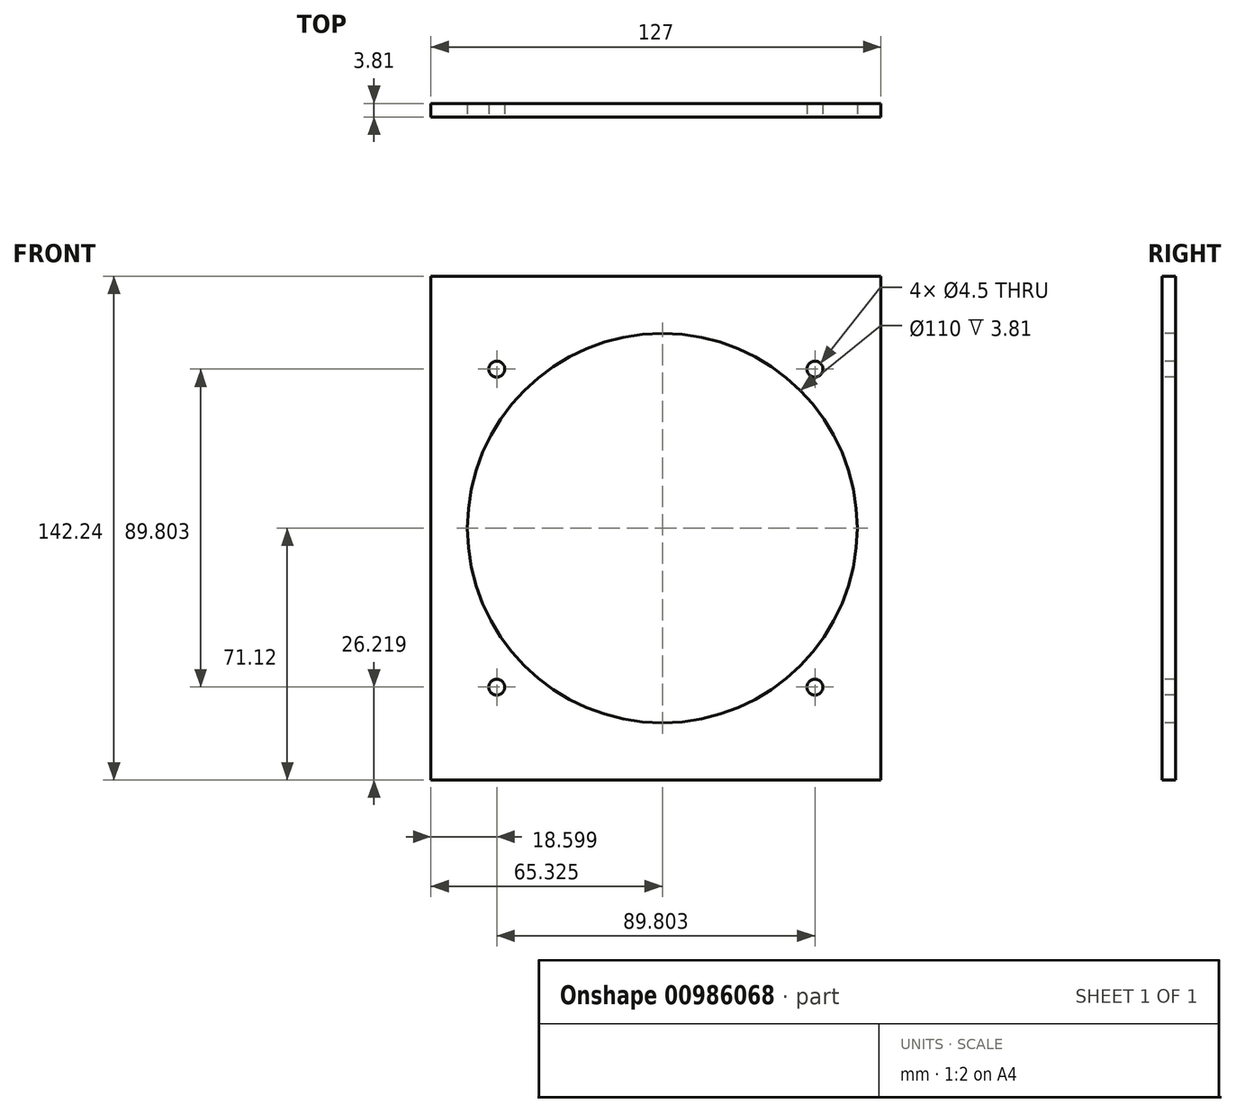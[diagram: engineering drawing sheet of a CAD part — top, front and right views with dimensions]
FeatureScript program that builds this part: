
annotation { "Feature Type Name" : "Feature", "Feature Type Description" : "" }
export const myFeature = defineFeature(function(context is Context, id is Id, definition is map)
    precondition{}
    {
        {
            var Q0;
            Q0=qCreatedBy(makeId("Front.planeOp"),FACE);
            var sketch = newSketch(context, id + "F0", { "sketchPlane" : qUnion([Q0])});
            skLineSegment(sketch, "E0.bottom", {"start": v(63.5, 71.12) * mm, "end": v(-63.5, 71.12) * mm});
            skLineSegment(sketch, "E0.top", {"start": v(63.5, -71.12) * mm, "end": v(-63.5, -71.12) * mm});
            skLineSegment(sketch, "E0.left", {"start": v(63.5, 71.12) * mm, "end": v(63.5, -71.12) * mm});
            skLineSegment(sketch, "E0.right", {"start": v(-63.5, 71.12) * mm, "end": v(-63.5, -71.12) * mm});
            skPoint(sketch, "E0.middle", {"position": v(0, 0) * mm});
            skSolve(sketch);
        }
        {
            var Q0;
            Q0=makeQuery(id+"F0.imprint","IMPRINT",FACE,{"disambiguationData":[TD([[makeQuery(id+"F0.imprint","IMPRINT",EDGE,{"derivedFrom":sQuery(id+"F0.wireOp",EDGE,"E0.bottom")}),1.0]])]});
            extrude(context, id + "F1", {"entities" : qUnion([Q0]), "depth" : 3.8 * mm, "offsetDistance" : 25.4 * mm});
        }
        {
            var Q0;
            Q0=makeQuery(id+"F1.opExtrude","CAP_FACE",FACE,{"disambiguationData":[OSD([sQuery(id+"F0.wireOp",EDGE,"E0.bottom"),sQuery(id+"F0.wireOp",EDGE,"E0.top"),sQuery(id+"F0.wireOp",EDGE,"E0.left"),sQuery(id+"F0.wireOp",EDGE,"E0.right")])],"isStart":false});
            var sketch = newSketch(context, id + "F2", { "sketchPlane" : qUnion([Q0])});
            skCircle(sketch, "E1", {"center": v(1.82, 0) * mm, "radius": 55 * mm});
            skSolve(sketch);
        }
        {
            var Q0;
            Q0=makeQuery(id+"F2.imprint","IMPRINT",FACE,{"disambiguationData":[TD([[makeQuery(id+"F2.imprint","IMPRINT",EDGE,{"derivedFrom":sQuery(id+"F2.wireOp",EDGE,"E1")}),1.0]])]});
            extrude(context, id + "F3", {"entities" : qUnion([Q0]), "operationType" : NewBodyOperationType.REMOVE, "endBound" : BoundingType.UP_TO_NEXT, "oppositeDirection" : true, "depth" : 25.4 * mm, "offsetDistance" : 25.4 * mm});
        }
        {
            var Q0;
            Q0=makeQuery(id+"F1.opExtrude","CAP_FACE",FACE,{"disambiguationData":[OSD([sQuery(id+"F0.wireOp",EDGE,"E0.bottom"),sQuery(id+"F0.wireOp",EDGE,"E0.top"),sQuery(id+"F0.wireOp",EDGE,"E0.left"),sQuery(id+"F0.wireOp",EDGE,"E0.right")])],"isStart":false});
            var sketch = newSketch(context, id + "F4", { "sketchPlane" : qUnion([Q0])});
            skCircle(sketch, "E2", {"center": v(0, 0) * mm, "radius": 63.5 * mm});
            skCircle(sketch, "E3", {"center": v(44.9, -44.9) * mm, "radius": 2.25 * mm});
            skCircle(sketch, "E4", {"center": v(-44.9, -44.9) * mm, "radius": 2.25 * mm});
            skCircle(sketch, "E5", {"center": v(-44.9, 44.9) * mm, "radius": 2.25 * mm});
            skCircle(sketch, "E6", {"center": v(44.9, 44.9) * mm, "radius": 2.25 * mm});
            skLineSegment(sketch, "E7", {"start": v(-44.9, 44.9) * mm, "end": v(0, 0) * mm});
            skLineSegment(sketch, "E8", {"start": v(44.9, 44.9) * mm, "end": v(0, 0) * mm});
            skLineSegment(sketch, "E9", {"start": v(0, 0) * mm, "end": v(44.9, -44.9) * mm});
            skLineSegment(sketch, "E10", {"start": v(0, 0) * mm, "end": v(-44.9, -44.9) * mm});
            skSolve(sketch);
        }
        {
            var Q0;
            {var subQ0=sQuery(id+"F4.wireOp",EDGE,"E7");var subQ1=sQuery(id+"F4.wireOp",EDGE,"E2");var subQ2=makeQuery(id+"F4.imprint","INTERSECT",VERTEX,{"derivedFrom":[subQ1,subQ0]});Q0=makeQuery(id+"F4.imprint","IMPRINT",FACE,{"disambiguationData":[TD([[makeQuery(id+"F4.imprint","IMPRINT",EDGE,{"disambiguationData":[TD([[subQ2,1.0]])],"derivedFrom":subQ1}),1.0]])]});}
            var Q1;
            {var subQ0=sQuery(id+"F4.wireOp",EDGE,"E2");var subQ1=makeQuery(id+"F4.imprint","INTERSECT",VERTEX,{"derivedFrom":[subQ0,sQuery(id+"F4.wireOp",EDGE,"E7")]});Q1=makeQuery(id+"F4.imprint","IMPRINT",FACE,{"disambiguationData":[TD([[makeQuery(id+"F4.imprint","IMPRINT",EDGE,{"disambiguationData":[TD([[subQ1,1.0]])],"derivedFrom":subQ0}),-1.0]])]});}
            var Q2;
            {var subQ0=sQuery(id+"F4.wireOp",EDGE,"E7");var subQ1=sQuery(id+"F4.wireOp",EDGE,"E2");var subQ2=makeQuery(id+"F4.imprint","INTERSECT",VERTEX,{"derivedFrom":[subQ1,subQ0]});Q2=makeQuery(id+"F4.imprint","IMPRINT",FACE,{"disambiguationData":[TD([[makeQuery(id+"F4.imprint","IMPRINT",EDGE,{"disambiguationData":[TD([[subQ2,-1.0]])],"derivedFrom":subQ1}),1.0]])]});}
            var Q3;
            {var subQ0=sQuery(id+"F4.wireOp",EDGE,"E2");var subQ1=makeQuery(id+"F4.imprint","INTERSECT",VERTEX,{"derivedFrom":[subQ0,sQuery(id+"F4.wireOp",EDGE,"E8")]});Q3=makeQuery(id+"F4.imprint","IMPRINT",FACE,{"disambiguationData":[TD([[makeQuery(id+"F4.imprint","IMPRINT",EDGE,{"disambiguationData":[TD([[subQ1,1.0]])],"derivedFrom":subQ0}),-1.0]])]});}
            var Q4;
            {var subQ0=sQuery(id+"F4.wireOp",EDGE,"E8");var subQ1=sQuery(id+"F4.wireOp",EDGE,"E2");var subQ2=makeQuery(id+"F4.imprint","INTERSECT",VERTEX,{"derivedFrom":[subQ1,subQ0]});Q4=makeQuery(id+"F4.imprint","IMPRINT",FACE,{"disambiguationData":[TD([[makeQuery(id+"F4.imprint","IMPRINT",EDGE,{"disambiguationData":[TD([[subQ2,-1.0]])],"derivedFrom":subQ1}),1.0]])]});}
            var Q5;
            {var subQ0=sQuery(id+"F4.wireOp",EDGE,"E8");var subQ1=sQuery(id+"F4.wireOp",EDGE,"E2");var subQ2=makeQuery(id+"F4.imprint","INTERSECT",VERTEX,{"derivedFrom":[subQ1,subQ0]});Q5=makeQuery(id+"F4.imprint","IMPRINT",FACE,{"disambiguationData":[TD([[makeQuery(id+"F4.imprint","IMPRINT",EDGE,{"disambiguationData":[TD([[subQ2,1.0]])],"derivedFrom":subQ1}),1.0]])]});}
            var Q6;
            {var subQ0=sQuery(id+"F4.wireOp",EDGE,"E9");var subQ1=sQuery(id+"F4.wireOp",EDGE,"E2");var subQ2=makeQuery(id+"F4.imprint","INTERSECT",VERTEX,{"derivedFrom":[subQ1,subQ0]});Q6=makeQuery(id+"F4.imprint","IMPRINT",FACE,{"disambiguationData":[TD([[makeQuery(id+"F4.imprint","IMPRINT",EDGE,{"disambiguationData":[TD([[subQ2,1.0]])],"derivedFrom":subQ1}),1.0]])]});}
            var Q7;
            {var subQ0=sQuery(id+"F4.wireOp",EDGE,"E9");var subQ1=sQuery(id+"F4.wireOp",EDGE,"E2");var subQ2=makeQuery(id+"F4.imprint","INTERSECT",VERTEX,{"derivedFrom":[subQ1,subQ0]});Q7=makeQuery(id+"F4.imprint","IMPRINT",FACE,{"disambiguationData":[TD([[makeQuery(id+"F4.imprint","IMPRINT",EDGE,{"disambiguationData":[TD([[subQ2,-1.0]])],"derivedFrom":subQ1}),1.0]])]});}
            var Q8;
            {var subQ0=sQuery(id+"F4.wireOp",EDGE,"E2");var subQ1=makeQuery(id+"F4.imprint","INTERSECT",VERTEX,{"derivedFrom":[subQ0,sQuery(id+"F4.wireOp",EDGE,"E9")]});Q8=makeQuery(id+"F4.imprint","IMPRINT",FACE,{"disambiguationData":[TD([[makeQuery(id+"F4.imprint","IMPRINT",EDGE,{"disambiguationData":[TD([[subQ1,1.0]])],"derivedFrom":subQ0}),-1.0]])]});}
            var Q9;
            {var subQ0=sQuery(id+"F4.wireOp",EDGE,"E2");var subQ1=makeQuery(id+"F4.imprint","INTERSECT",VERTEX,{"derivedFrom":[subQ0,sQuery(id+"F4.wireOp",EDGE,"E10")]});Q9=makeQuery(id+"F4.imprint","IMPRINT",FACE,{"disambiguationData":[TD([[makeQuery(id+"F4.imprint","IMPRINT",EDGE,{"disambiguationData":[TD([[subQ1,1.0]])],"derivedFrom":subQ0}),-1.0]])]});}
            var Q10;
            {var subQ0=sQuery(id+"F4.wireOp",EDGE,"E10");var subQ1=sQuery(id+"F4.wireOp",EDGE,"E2");var subQ2=makeQuery(id+"F4.imprint","INTERSECT",VERTEX,{"derivedFrom":[subQ1,subQ0]});Q10=makeQuery(id+"F4.imprint","IMPRINT",FACE,{"disambiguationData":[TD([[makeQuery(id+"F4.imprint","IMPRINT",EDGE,{"disambiguationData":[TD([[subQ2,-1.0]])],"derivedFrom":subQ1}),1.0]])]});}
            var Q11;
            {var subQ0=sQuery(id+"F4.wireOp",EDGE,"E10");var subQ1=sQuery(id+"F4.wireOp",EDGE,"E2");var subQ2=makeQuery(id+"F4.imprint","INTERSECT",VERTEX,{"derivedFrom":[subQ1,subQ0]});Q11=makeQuery(id+"F4.imprint","IMPRINT",FACE,{"disambiguationData":[TD([[makeQuery(id+"F4.imprint","IMPRINT",EDGE,{"disambiguationData":[TD([[subQ2,1.0]])],"derivedFrom":subQ1}),1.0]])]});}
            extrude(context, id + "F5", {"entities" : qUnion([Q0, Q1, Q2, Q3, Q4, Q5, Q6, Q7, Q8, Q9, Q10, Q11]), "operationType" : NewBodyOperationType.REMOVE, "endBound" : BoundingType.UP_TO_NEXT, "oppositeDirection" : true, "depth" : 25.4 * mm, "offsetDistance" : 25.4 * mm});
        }
    });
